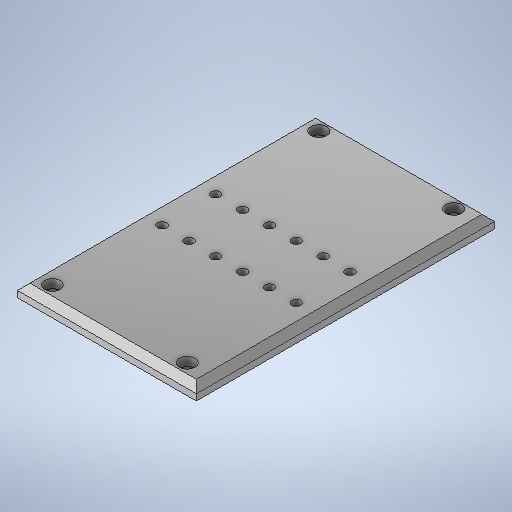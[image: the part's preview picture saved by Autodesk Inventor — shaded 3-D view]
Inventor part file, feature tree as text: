
AUTODESK INVENTOR PART (.ipt)
format: ipt  version: 2025 (Build 290162000, 162)  size: 291,840 bytes
history: native  units: mm
features: sketch x4, hole x2, extrude x1, chamfer x1
ambient origin geometry x8: Origin, YZ Plane, XZ Plane, XY Plane, X Axis, Y Axis, Z Axis, Center Point
bodies: Solid1 (feature_tree)
feature tree (8):
  extrude  "Extrusion1"  Depth=90.0mm
  chamfer  "Chamfer1"  Distance=6.35mm
  hole  "Hole1"  [1 undecoded]
  hole  "Hole2"  [1 undecoded]
  sketch  "Sketch1"  dims[d0=150.0mm d1=90.0mm d2=6.35mm d3=0.0mm]
  sketch  "Sketch3"  dims[d8=8.0mm d9=8.0mm]
  sketch  "Sketch4"  dims[d10=12.6mm d11=4.7mm d12=5.984mm d13=7.9mm d14=4.4mm d15=14.3117mm d16=7.9mm d17=20.594885mm d18=27.0mm d19=13.5mm d20=60.0mm d22=13.5mm d23=10.0mm d25=10.0mm d27=4.5mm d28=6.0mm d29=9.4mm d30=3.58mm d31=90.0deg d32=7.9mm d33=20.594885mm d34=6.75mm]
  sketch  "Sketch Rectangular Pattern1"  dims[d4=3.175mm d5=2.0mm d6=45.0deg d7=9.6mm]
note: 2 required parameter values undecoded (feature->parameter linkage not recoverable at this tier; creation-order binding heuristic only, values carry confidence <= 0.55)
